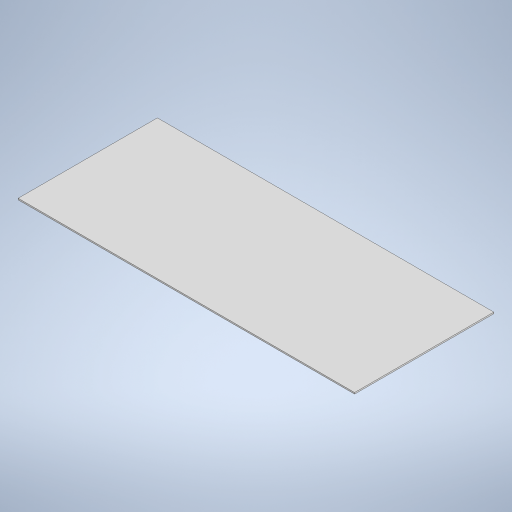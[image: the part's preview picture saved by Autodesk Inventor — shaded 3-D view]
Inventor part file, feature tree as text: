
AUTODESK INVENTOR PART (.ipt)
format: ipt  version: 2023 (Build 270158000, 158)  size: 207,360 bytes
history: native  units: in
note: dims shown in document units (in); Inventor stores cm internally (conversion verified against a paired STEP export)
features: extrude x1, sketch x1
ambient origin geometry x8: Origin, YZ Plane, XZ Plane, XY Plane, X Axis, Y Axis, Z Axis, Center Point
bodies: Solid1 (feature_tree)
feature tree (2):
  extrude  "Extrusion1"  Depth=14.5in
  sketch  "Sketch1"  dims[d0=6.0in d1=14.5in d2=0.0625in d3=0.0in]
